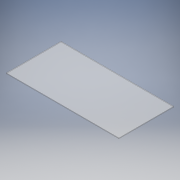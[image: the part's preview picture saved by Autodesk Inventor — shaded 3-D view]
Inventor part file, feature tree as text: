
AUTODESK INVENTOR PART (.ipt)
format: ipt  version: 2018 (Build 220112000, 112)  size: 97,280 bytes
history: native  units: mm
features: other x1, extrude x1, sketch x1
ambient origin geometry x8: Origin, YZ Plane, XZ Plane, XY Plane, X Axis, Y Axis, Z Axis, Center Point
bodies: Body1 (feature_tree)
feature tree (3):
  other  "ソリッド1"
  extrude  "押し出し1"  Depth=617.066667mm
  sketch  "スケッチ1"
